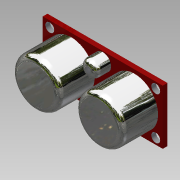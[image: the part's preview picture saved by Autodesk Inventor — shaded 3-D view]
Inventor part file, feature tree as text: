
AUTODESK INVENTOR PART (.ipt)
format: ipt  version: 2015 SP1 (Build 190203100, 203)  size: 201,216 bytes
history: native  units: mm
features: extrude x6, sketch x3, fillet x2
ambient origin geometry x8: Origin, YZ Plane, XZ Plane, XY Plane, X Axis, Y Axis, Z Axis, Center Point
bodies: Solid1 (feature_tree)
feature tree (11):
  sketch  "Sketch1"  dims[d0=43.21mm d1=19.7mm]
  extrude  "Extrusion1"  Depth=19.7mm
  extrude  "Extrusion2"  Depth=3.2mm
  extrude  "Extrusion3"  Depth=10.0mm
  extrude  "Extrusion4"  Depth=10.0mm
  extrude  "Extrusion5"  Depth=1.7mm TaperAngle=0.0deg
  fillet  "Fillet1"  Radius=14.6mm
  fillet  "Fillet2"  Radius=7.07mm
  extrude  "Extrusion6"  Depth=5.2mm
  sketch  "Sketch3"  dims[d8=17.0mm d9=17.0mm d14=6.0mm d16=1.7mm d17=0.0mm d18=14.6mm d19=0.0mm d20=7.07mm d21=0.0mm d22=5.2mm d23=10.13mm d24=2.0mm d25=0.0mm d26=1.27mm d27=1.27mm d28=1.27mm d29=1.27mm d30=1.27mm d31=2.54mm d32=2.54mm d33=2.54mm d34=2.54mm d35=2.0mm d36=0.0mm d37=2.0mm d38=2.0mm d41=22.86mm d43=10.175mm d44=10.175mm d45=6.54mm d47=7.874mm d48=7.654mm d49=7.654mm d50=7.654mm d51=7.654mm d52=90.0deg d53=180.0deg d54=10.0mm d55=0.0mm]
  sketch  "Sketch2"  dims[d2=3.2mm d5=3.2mm]
